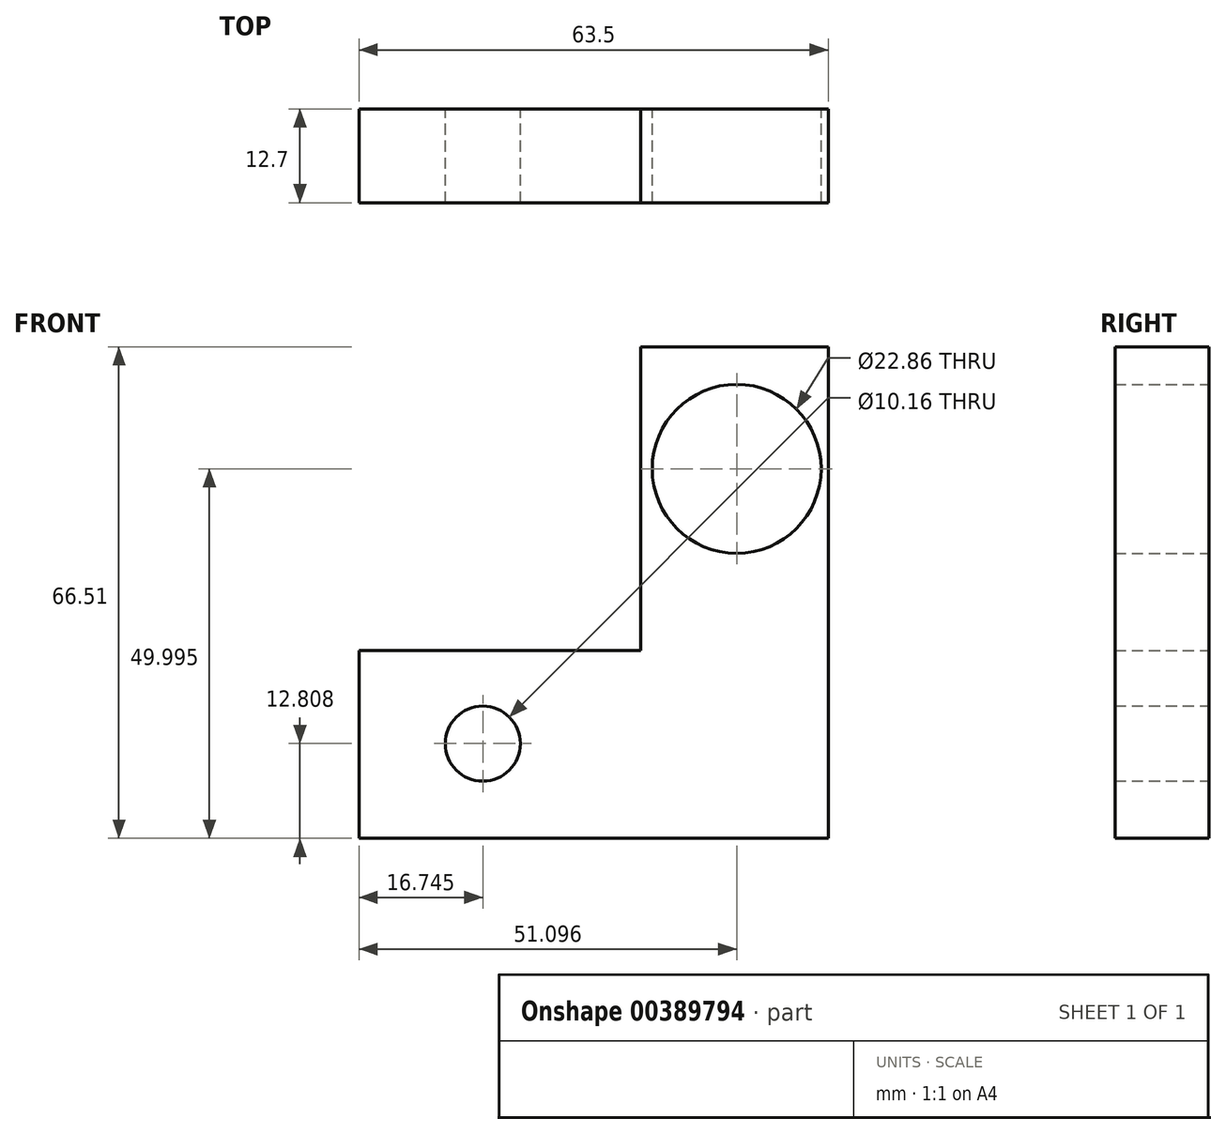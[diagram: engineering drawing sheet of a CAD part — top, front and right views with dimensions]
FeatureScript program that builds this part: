
annotation { "Feature Type Name" : "Feature", "Feature Type Description" : "" }
export const myFeature = defineFeature(function(context is Context, id is Id, definition is map)
    precondition{}
    {
        {
            var Q0;
            Q0=qCreatedBy(makeId("Front.planeOp"),FACE);
            var sketch = newSketch(context, id + "F0", { "sketchPlane" : qUnion([Q0])});
            skLineSegment(sketch, "E0.bottom", {"start": v(0.28, 31.28) * mm, "end": v(25.68, 31.28) * mm});
            skLineSegment(sketch, "E0.top", {"start": v(0.28, -35.23) * mm, "end": v(25.68, -35.23) * mm});
            skLineSegment(sketch, "E0.left", {"start": v(0.28, 31.28) * mm, "end": v(0.28, -9.83) * mm});
            skLineSegment(sketch, "E0.right", {"start": v(25.68, 31.28) * mm, "end": v(25.68, -35.23) * mm});
            skLineSegment(sketch, "E1.bottom", {"start": v(0.28, -9.83) * mm, "end": v(-37.82, -9.83) * mm});
            skLineSegment(sketch, "E1.top", {"start": v(25.68, -35.23) * mm, "end": v(-37.82, -35.23) * mm});
            skLineSegment(sketch, "E1.right", {"start": v(-37.82, -9.83) * mm, "end": v(-37.82, -35.23) * mm});
            skCircle(sketch, "E2", {"center": v(13.28, 14.77) * mm, "radius": 11.43 * mm});
            skCircle(sketch, "E3", {"center": v(-21.07, -22.42) * mm, "radius": 5.08 * mm});
            skSolve(sketch);
        }
        {
            var Q0;
            Q0 = qSketchRegion(id + "F0", true);
            extrude(context, id + "F1", {"entities" : qUnion([Q0]), "depth" : 12.7 * mm});
        }
    });
